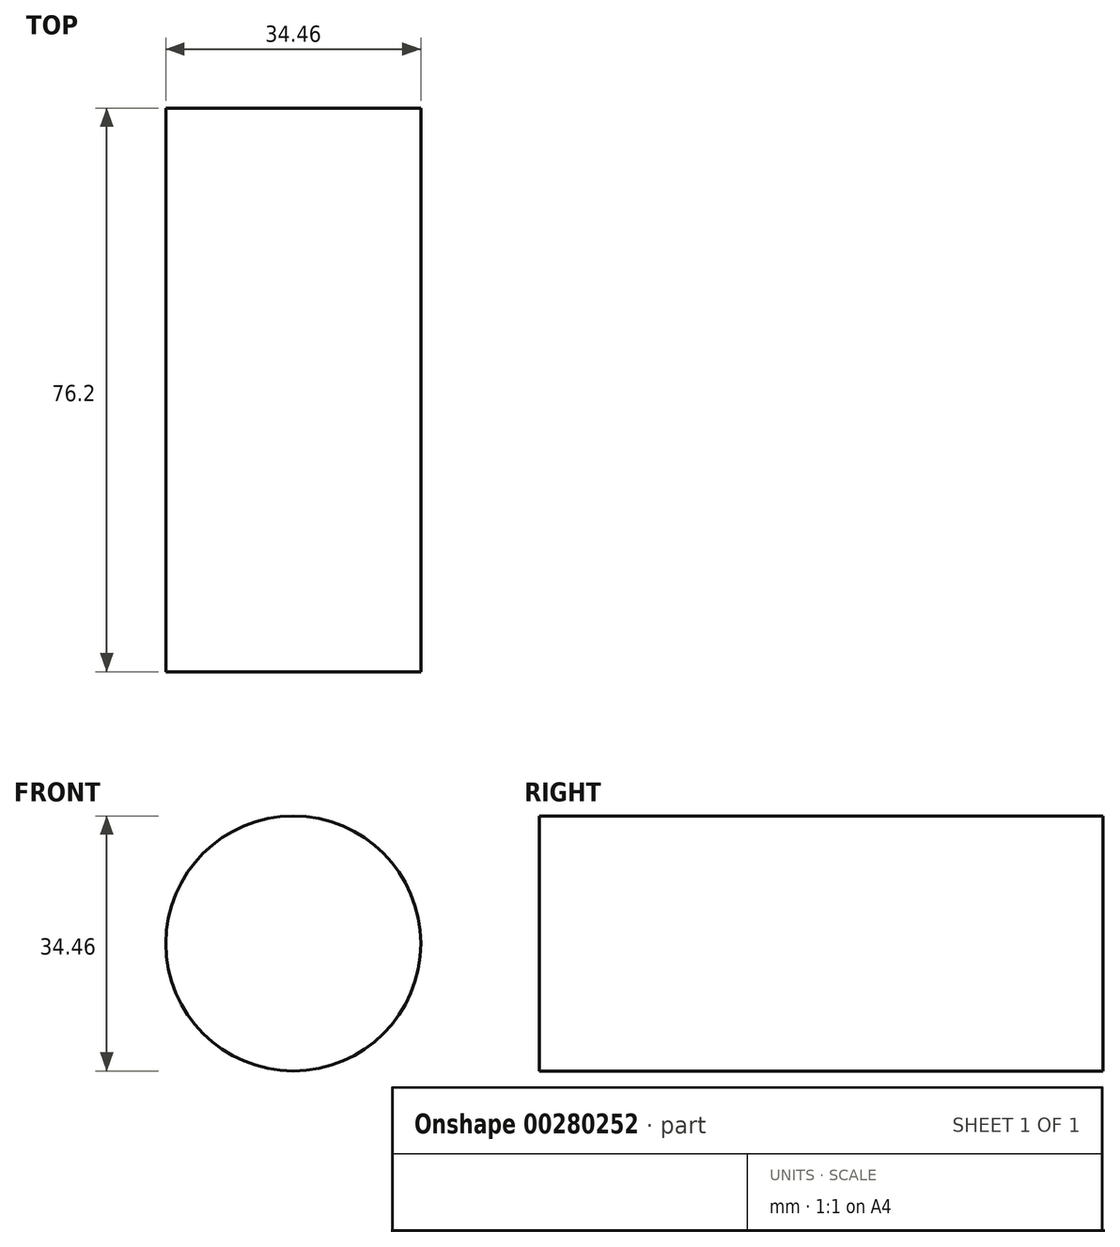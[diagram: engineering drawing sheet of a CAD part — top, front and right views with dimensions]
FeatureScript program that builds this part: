
annotation { "Feature Type Name" : "Feature", "Feature Type Description" : "" }
export const myFeature = defineFeature(function(context is Context, id is Id, definition is map)
    precondition{}
    {
        {
            var Q0;
            Q0=qCreatedBy(makeId("Front.planeOp"),FACE);
            var sketch = newSketch(context, id + "F0", { "sketchPlane" : qUnion([Q0])});
            skCircle(sketch, "E0", {"center": v(0, 0) * mm, "radius": 17.23 * mm});
            skSolve(sketch);
        }
        {
            var Q0;
            Q0 = qSketchRegion(id + "F0", true);
            extrude(context, id + "F1", {"entities" : qUnion([Q0]), "depth" : 76.2 * mm});
        }
    });
